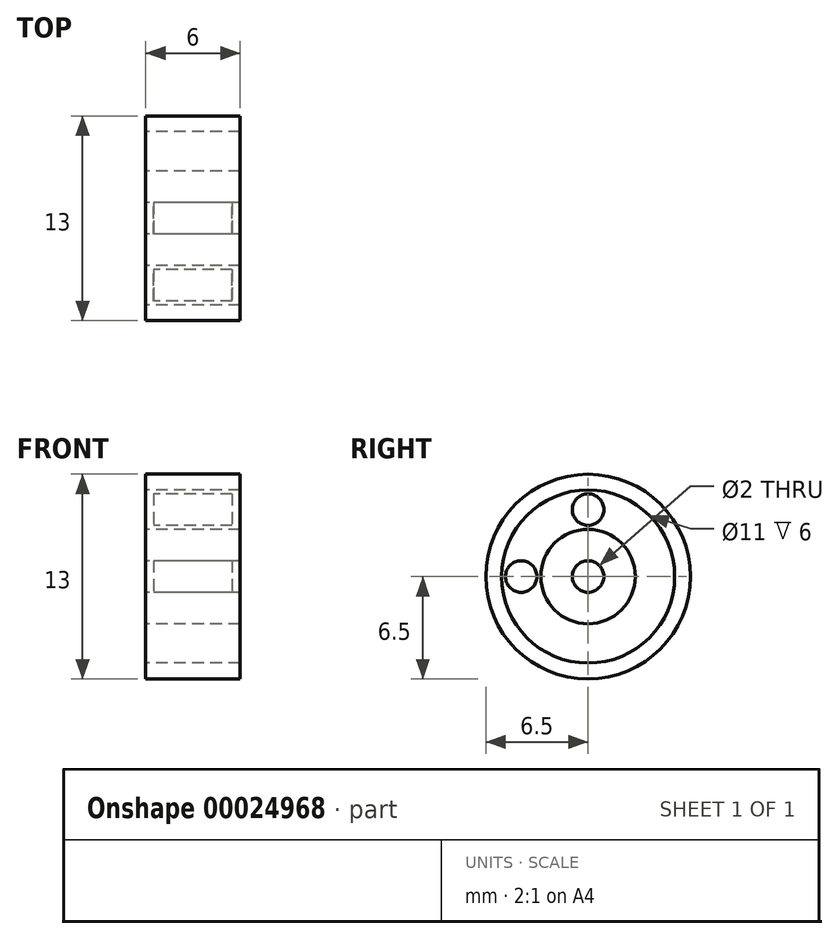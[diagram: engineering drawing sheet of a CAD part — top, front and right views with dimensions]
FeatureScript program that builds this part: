
annotation { "Feature Type Name" : "Feature", "Feature Type Description" : "" }
export const myFeature = defineFeature(function(context is Context, id is Id, definition is map)
    precondition{}
    {
        {
            var Q0;
            Q0=qCreatedBy(makeId("Front.planeOp"),FACE);
            var sketch = newSketch(context, id + "F0", { "sketchPlane" : qUnion([Q0])});
            skLineSegment(sketch, "E0", {"start": v(-14.01, 0) * mm, "end": v(14.24, 0) * mm, "construction": true});
            skLineSegment(sketch, "E1", {"start": v(0, 0) * mm, "end": v(0, 1) * mm, "construction": true});
            skLineSegment(sketch, "E2.rect.bottom", {"start": v(-3, 1) * mm, "end": v(3, 1) * mm});
            skLineSegment(sketch, "E2.rect.top", {"start": v(-3, 3) * mm, "end": v(3, 3) * mm});
            skLineSegment(sketch, "E2.rect.left", {"start": v(-3, 1) * mm, "end": v(-3, 3) * mm});
            skLineSegment(sketch, "E2.rect.right", {"start": v(3, 1) * mm, "end": v(3, 3) * mm});
            skPoint(sketch, "E2.rect.middle", {"position": v(0, 2) * mm});
            skLineSegment(sketch, "E3.rect.bottom", {"start": v(-2.5, 3) * mm, "end": v(2.5, 3) * mm});
            skLineSegment(sketch, "E3.rect.top", {"start": v(-2.5, 5.5) * mm, "end": v(2.5, 5.5) * mm});
            skLineSegment(sketch, "E3.rect.left", {"start": v(-2.5, 3) * mm, "end": v(-2.5, 5.5) * mm});
            skLineSegment(sketch, "E3.rect.right", {"start": v(2.5, 3) * mm, "end": v(2.5, 5.5) * mm});
            skPoint(sketch, "E3.rect.middle", {"position": v(0, 4.25) * mm});
            skLineSegment(sketch, "E4.rect.bottom", {"start": v(-3, 5.5) * mm, "end": v(3, 5.5) * mm});
            skLineSegment(sketch, "E4.rect.top", {"start": v(-3, 6.5) * mm, "end": v(3, 6.5) * mm});
            skLineSegment(sketch, "E4.rect.left", {"start": v(-3, 5.5) * mm, "end": v(-3, 6.5) * mm});
            skLineSegment(sketch, "E4.rect.right", {"start": v(3, 5.5) * mm, "end": v(3, 6.5) * mm});
            skPoint(sketch, "E4.rect.middle", {"position": v(0, 6) * mm});
            skSolve(sketch);
        }
        {
            var Q0;
            Q0 = qSketchRegion(id + "F0", true);
            var Q1;
            Q1=sQuery(id+"F0.wireOp",EDGE,"E0");
            revolve(context, id + "F1", {"entities" : qUnion([Q0]), "axis" : qUnion([Q1]), "revolveType" : RevolveType.FULL});
        }
        {
            var Q0;
            Q0=makeQuery(id+"F1.opRevolve","SWEPT_FACE",FACE,{"disambiguationData":[OSD([sQuery(id+"F0.wireOp",EDGE,"E3.rect.left")])]});
            var sketch = newSketch(context, id + "F2", { "sketchPlane" : qUnion([Q0])});
            skCircle(sketch, "E5", {"center": v(0, 0) * mm, "radius": 4.25 * mm});
            skCircle(sketch, "E6", {"center": v(0, 4.25) * mm, "radius": 1 * mm});
            skCircle(sketch, "E7.1.0", {"center": v(-4.25, 0) * mm, "radius": 1 * mm});
            skCircle(sketch, "E7.2.0", {"center": v(0, -4.25) * mm, "radius": 1 * mm});
            skCircle(sketch, "E7.3.0", {"center": v(4.25, 0) * mm, "radius": 1 * mm});
            skSolve(sketch);
        }
        {
            var Q0;
            {var subQ0=sQuery(id+"F2.wireOp",EDGE,"E6");var subQ1=sQuery(id+"F2.wireOp",EDGE,"E5");var subQ3=makeQuery(id+"F2.imprint","INTERSECT",VERTEX,{"disambiguationData":[OD(0.0)],"derivedFrom":[subQ1,subQ0]});Q0=makeQuery(id+"F2.imprint","IMPRINT",FACE,{"disambiguationData":[TD([[makeQuery(id+"F2.imprint","IMPRINT",EDGE,{"disambiguationData":[TD([[subQ3,-1.0]])],"derivedFrom":subQ1}),-1.0]])]});}
            var Q1;
            {var subQ0=sQuery(id+"F2.wireOp",EDGE,"E6");var subQ1=sQuery(id+"F2.wireOp",EDGE,"E5");var subQ3=makeQuery(id+"F2.imprint","INTERSECT",VERTEX,{"disambiguationData":[OD(0.0)],"derivedFrom":[subQ1,subQ0]});Q1=makeQuery(id+"F2.imprint","IMPRINT",FACE,{"disambiguationData":[TD([[makeQuery(id+"F2.imprint","IMPRINT",EDGE,{"disambiguationData":[TD([[subQ3,-1.0]])],"derivedFrom":subQ1}),1.0]])]});}
            var Q2;
            {var subQ0=sQuery(id+"F2.wireOp",EDGE,"E7.1.0");var subQ1=sQuery(id+"F2.wireOp",EDGE,"E5");var subQ3=makeQuery(id+"F2.imprint","INTERSECT",VERTEX,{"disambiguationData":[OD(0.0)],"derivedFrom":[subQ1,subQ0]});Q2=makeQuery(id+"F2.imprint","IMPRINT",FACE,{"disambiguationData":[TD([[makeQuery(id+"F2.imprint","IMPRINT",EDGE,{"disambiguationData":[TD([[subQ3,-1.0]])],"derivedFrom":subQ1}),-1.0]])]});}
            var Q3;
            {var subQ0=sQuery(id+"F2.wireOp",EDGE,"E7.1.0");var subQ1=sQuery(id+"F2.wireOp",EDGE,"E5");var subQ3=makeQuery(id+"F2.imprint","INTERSECT",VERTEX,{"disambiguationData":[OD(0.0)],"derivedFrom":[subQ1,subQ0]});Q3=makeQuery(id+"F2.imprint","IMPRINT",FACE,{"disambiguationData":[TD([[makeQuery(id+"F2.imprint","IMPRINT",EDGE,{"disambiguationData":[TD([[subQ3,-1.0]])],"derivedFrom":subQ1}),1.0]])]});}
            var Q4;
            {var subQ0=sQuery(id+"F2.wireOp",EDGE,"E7.2.0");var subQ1=sQuery(id+"F2.wireOp",EDGE,"E5");var subQ3=makeQuery(id+"F2.imprint","INTERSECT",VERTEX,{"disambiguationData":[OD(0.0)],"derivedFrom":[subQ1,subQ0]});Q4=makeQuery(id+"F2.imprint","IMPRINT",FACE,{"disambiguationData":[TD([[makeQuery(id+"F2.imprint","IMPRINT",EDGE,{"disambiguationData":[TD([[subQ3,-1.0]])],"derivedFrom":subQ1}),1.0]])]});}
            var Q5;
            {var subQ0=sQuery(id+"F2.wireOp",EDGE,"E7.2.0");var subQ1=sQuery(id+"F2.wireOp",EDGE,"E5");var subQ3=makeQuery(id+"F2.imprint","INTERSECT",VERTEX,{"disambiguationData":[OD(0.0)],"derivedFrom":[subQ1,subQ0]});Q5=makeQuery(id+"F2.imprint","IMPRINT",FACE,{"disambiguationData":[TD([[makeQuery(id+"F2.imprint","IMPRINT",EDGE,{"disambiguationData":[TD([[subQ3,-1.0]])],"derivedFrom":subQ1}),-1.0]])]});}
            var Q6;
            {var subQ0=sQuery(id+"F2.wireOp",EDGE,"E7.3.0");var subQ1=sQuery(id+"F2.wireOp",EDGE,"E5");var subQ3=makeQuery(id+"F2.imprint","INTERSECT",VERTEX,{"disambiguationData":[OD(0.0)],"derivedFrom":[subQ1,subQ0]});Q6=makeQuery(id+"F2.imprint","IMPRINT",FACE,{"disambiguationData":[TD([[makeQuery(id+"F2.imprint","IMPRINT",EDGE,{"disambiguationData":[TD([[subQ3,1.0]])],"derivedFrom":subQ1}),1.0]])]});}
            var Q7;
            {var subQ0=sQuery(id+"F2.wireOp",EDGE,"E7.3.0");var subQ1=sQuery(id+"F2.wireOp",EDGE,"E5");var subQ3=makeQuery(id+"F2.imprint","INTERSECT",VERTEX,{"disambiguationData":[OD(0.0)],"derivedFrom":[subQ1,subQ0]});Q7=makeQuery(id+"F2.imprint","IMPRINT",FACE,{"disambiguationData":[TD([[makeQuery(id+"F2.imprint","IMPRINT",EDGE,{"disambiguationData":[TD([[subQ3,1.0]])],"derivedFrom":subQ1}),-1.0]])]});}
            extrude(context, id + "F3", {"entities" : qUnion([Q0, Q1, Q2, Q3, Q4, Q5, Q6, Q7]), "operationType" : NewBodyOperationType.REMOVE, "endBound" : BoundingType.THROUGH_ALL, "oppositeDirection" : true, "depth" : 25.4 * mm});
        }
    });
